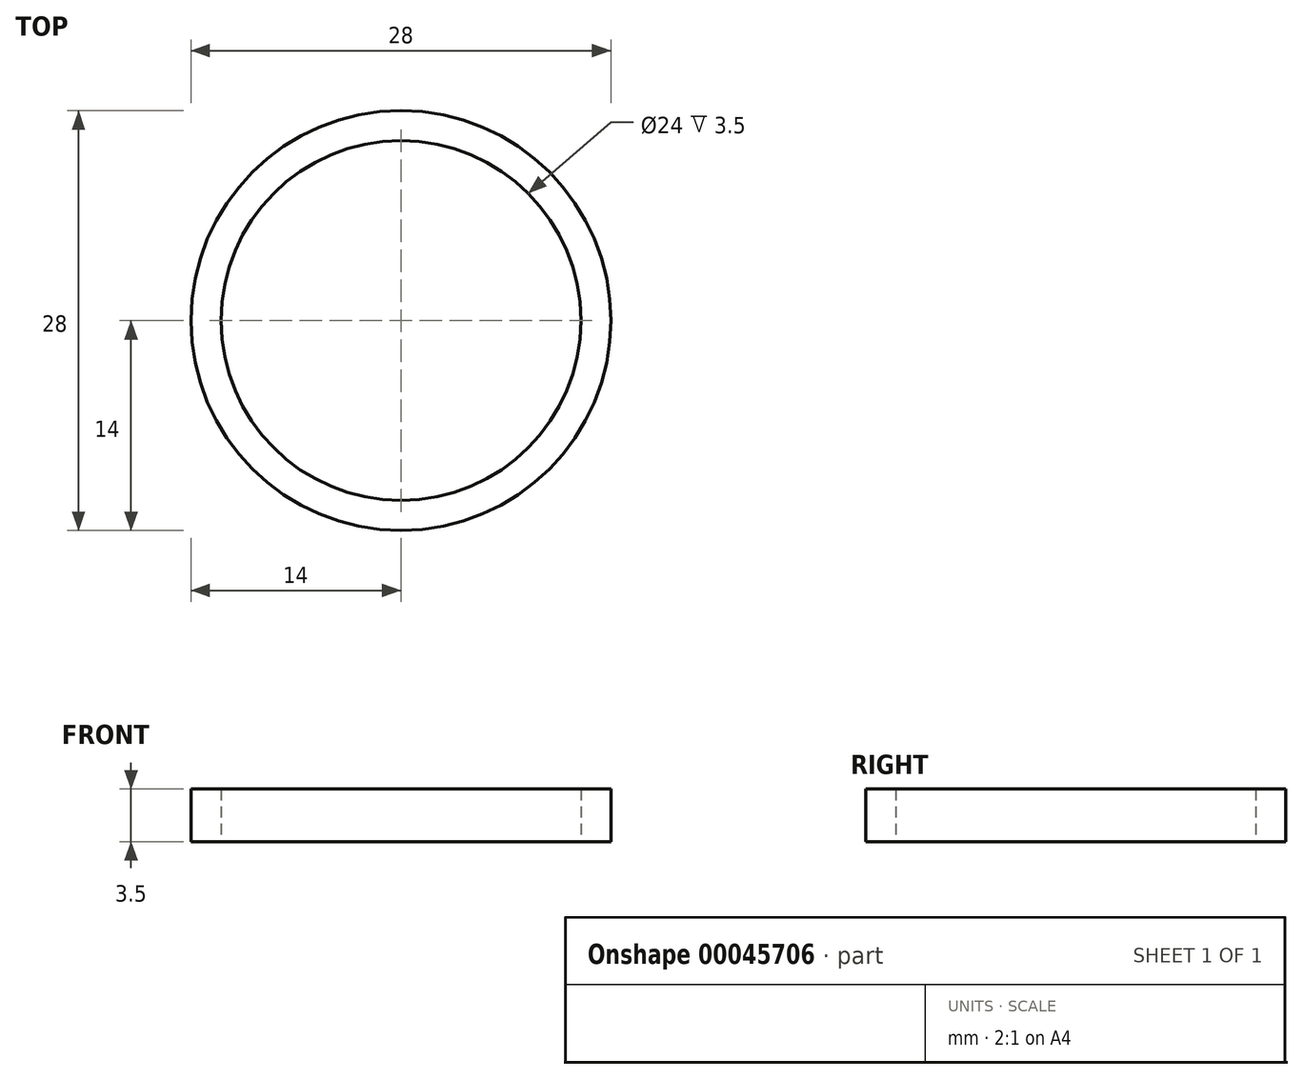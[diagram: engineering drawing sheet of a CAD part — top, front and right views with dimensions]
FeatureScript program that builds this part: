
annotation { "Feature Type Name" : "Feature", "Feature Type Description" : "" }
export const myFeature = defineFeature(function(context is Context, id is Id, definition is map)
    precondition{}
    {
        {
            var Q0;
            Q0=qCreatedBy(makeId("Top.planeOp"),FACE);
            var sketch = newSketch(context, id + "F0", { "sketchPlane" : qUnion([Q0])});
            skCircle(sketch, "E0", {"center": v(0, 0) * mm, "radius": 14 * mm});
            skSolve(sketch);
        }
        {
            var Q0;
            Q0=qSketchRegion(id+"F0",true);
            extrude(context, id + "F1", {"entities" : qUnion([Q0]), "depth" : 3.5 * mm});
        }
        {
            var Q0;
            Q0=makeQuery(id+"F1.opExtrude","CAP_FACE",FACE,{"disambiguationData":[OSD([sQuery(id+"F0.wireOp",EDGE,"E0")])],"isStart":false});
            var Q1;
            Q1=makeQuery(id+"F1.opExtrude","CAP_FACE",FACE,{"disambiguationData":[OSD([sQuery(id+"F0.wireOp",EDGE,"E0")])],"isStart":true});
            shell(context, id + "F2", {"entities" : qUnion([Q0, Q1]), "thickness" : 2 * mm});
        }
    });
